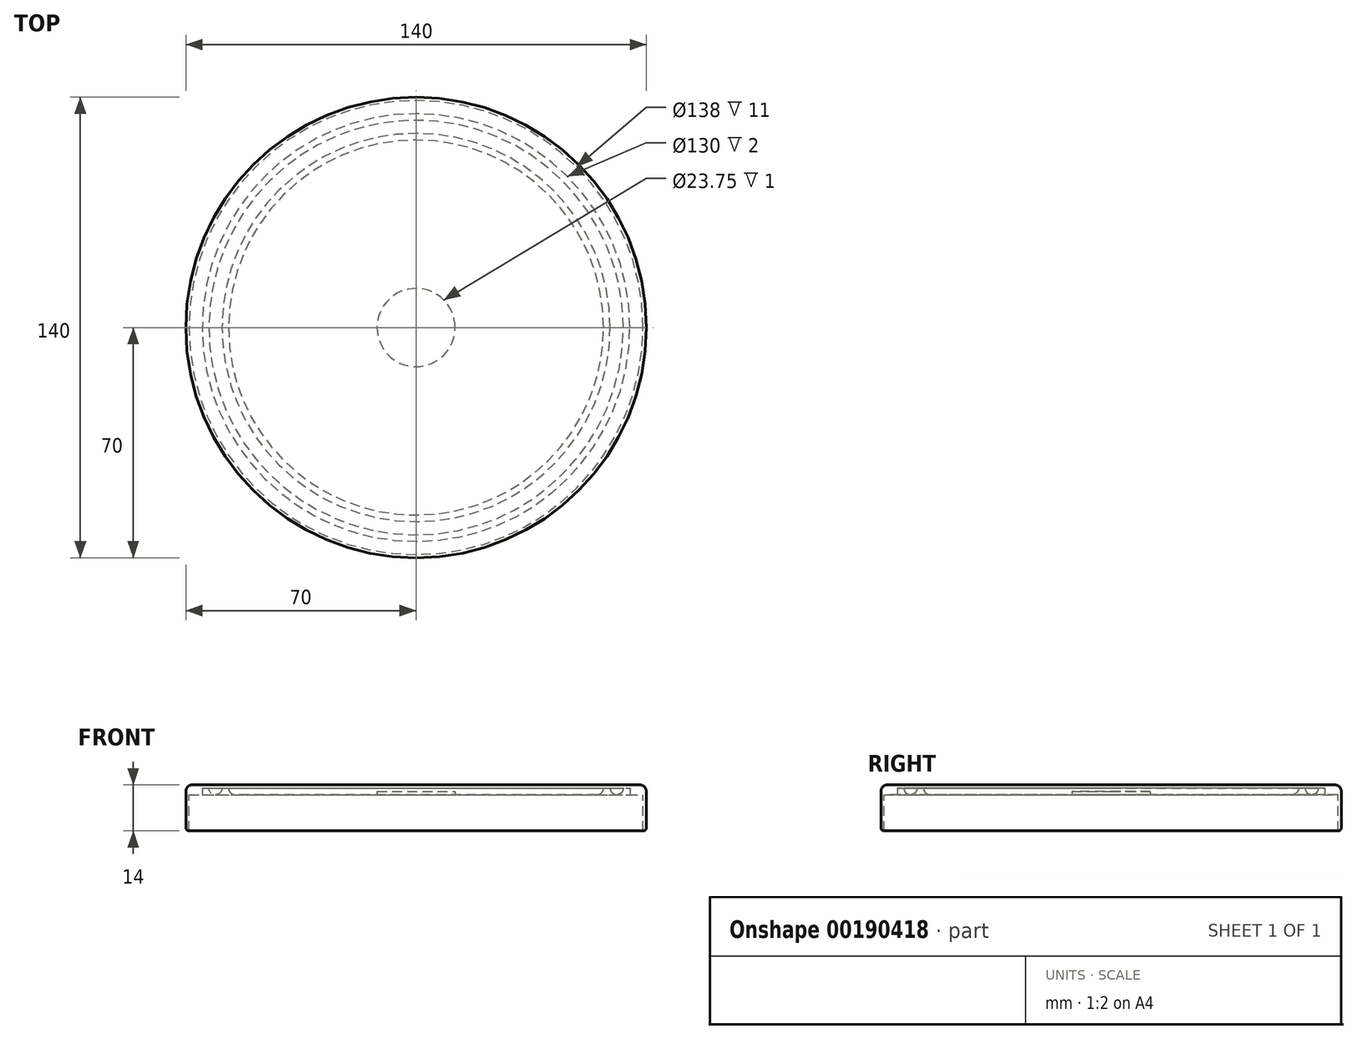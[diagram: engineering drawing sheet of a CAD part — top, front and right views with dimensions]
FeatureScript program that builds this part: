
annotation { "Feature Type Name" : "Feature", "Feature Type Description" : "" }
export const myFeature = defineFeature(function(context is Context, id is Id, definition is map)
    precondition{}
    {
        {
            var Q0;
            Q0=qCreatedBy(makeId("Top.planeOp"),FACE);
            var sketch = newSketch(context, id + "F0", { "sketchPlane" : qUnion([Q0])});
            skCircle(sketch, "E0", {"center": v(0, 0) * mm, "radius": 70 * mm});
            skSolve(sketch);
        }
        {
            var Q0;
            Q0 = qSketchRegion(id + "F0", true);
            extrude(context, id + "F1", {"entities" : qUnion([Q0]), "depth" : 3 * mm});
        }
        {
            var Q0;
            Q0=makeQuery(id+"F1.opExtrude","CAP_FACE",FACE,{"disambiguationData":[OSD([sQuery(id+"F0.wireOp",EDGE,"E0")])],"isStart":true});
            var sketch = newSketch(context, id + "F2", { "sketchPlane" : qUnion([Q0])});
            skCircle(sketch, "E1", {"center": v(0, 0) * mm, "radius": 69 * mm});
            skSolve(sketch);
        }
        {
            var Q0;
            Q0=makeQuery(id+"F2.imprint","IMPRINT",FACE,{"disambiguationData":[TD([[makeQuery(id+"F2.imprint","IMPRINT",EDGE,{"derivedFrom":sQuery(id+"F2.wireOp",EDGE,"E1")}),-1.0]])]});
            extrude(context, id + "F3", {"entities" : qUnion([Q0]), "operationType" : NewBodyOperationType.ADD, "depth" : 11 * mm});
        }
        {
            var Q0;
            Q0=makeQuery(id+"F1.opExtrude","CAP_EDGE",EDGE,{"disambiguationData":[OSD([sQuery(id+"F0.wireOp",EDGE,"E0")])],"isStart":false});
            fillet(context, id + "F4", {"entities" : qUnion([Q0]), "radius" : 2 * mm, "tangentPropagation" : true, "allowEdgeOverflow" : false});
        }
        {
            var Q0;
            Q0=makeQuery(id+"F1.opExtrude","CAP_FACE",FACE,{"disambiguationData":[OSD([sQuery(id+"F0.wireOp",EDGE,"E0")])],"isStart":true});
            var sketch = newSketch(context, id + "F5", { "sketchPlane" : qUnion([Q0])});
            skCircle(sketch, "E2", {"center": v(0, 0) * mm, "radius": 65 * mm});
            skCircle(sketch, "E3", {"center": v(0, 0) * mm, "radius": 63 * mm});
            skCircle(sketch, "E4", {"center": v(0, 0) * mm, "radius": 59 * mm});
            skCircle(sketch, "E5", {"center": v(0, 0) * mm, "radius": 57 * mm});
            skSolve(sketch);
        }
        {
            var Q0;
            Q0=makeQuery(id+"F5.imprint","IMPRINT",FACE,{"disambiguationData":[TD([[makeQuery(id+"F5.imprint","IMPRINT",EDGE,{"derivedFrom":sQuery(id+"F5.wireOp",EDGE,"E2")}),1.0]])]});
            var Q1;
            Q1=makeQuery(id+"F5.imprint","IMPRINT",FACE,{"disambiguationData":[TD([[makeQuery(id+"F5.imprint","IMPRINT",EDGE,{"derivedFrom":sQuery(id+"F5.wireOp",EDGE,"E4")}),1.0]])]});
            extrude(context, id + "F6", {"entities" : qUnion([Q0, Q1]), "operationType" : NewBodyOperationType.REMOVE, "oppositeDirection" : true, "depth" : 2 * mm});
        }
        {
            var Q0;
            Q0=makeQuery(id+"F6.boolean.opBoolean","COPY",EDGE,{"derivedFrom":makeQuery(id+"F6.opExtrude","CAP_EDGE",EDGE,{"disambiguationData":[OSD([sQuery(id+"F5.wireOp",EDGE,"E2")])],"isStart":true})});
            var Q1;
            Q1=makeQuery(id+"F6.boolean.opBoolean","COPY",EDGE,{"derivedFrom":makeQuery(id+"F6.opExtrude","CAP_EDGE",EDGE,{"disambiguationData":[OSD([sQuery(id+"F5.wireOp",EDGE,"E3")])],"isStart":true})});
            var Q2;
            Q2=makeQuery(id+"F6.boolean.opBoolean","COPY",EDGE,{"derivedFrom":makeQuery(id+"F6.opExtrude","CAP_EDGE",EDGE,{"disambiguationData":[OSD([sQuery(id+"F5.wireOp",EDGE,"E4")])],"isStart":true})});
            var Q3;
            Q3=makeQuery(id+"F6.boolean.opBoolean","COPY",EDGE,{"derivedFrom":makeQuery(id+"F6.opExtrude","CAP_EDGE",EDGE,{"disambiguationData":[OSD([sQuery(id+"F5.wireOp",EDGE,"E5")])],"isStart":true})});
            fillet(context, id + "F7", {"entities" : qUnion([Q0, Q1, Q2, Q3]), "radius" : 2 * mm, "tangentPropagation" : true, "allowEdgeOverflow" : false});
        }
        {
            var Q0;
            Q0=makeQuery(id+"F3.opExtrude","CAP_EDGE",EDGE,{"disambiguationData":[OSD([sQuery(id+"F0.wireOp",EDGE,"E0")])],"isStart":false});
            fillet(context, id + "F8", {"entities" : qUnion([Q0]), "radius" : 1 * mm, "tangentPropagation" : true, "allowEdgeOverflow" : false});
        }
        {
            var Q0;
            Q0=makeQuery(id+"F6.boolean.opBoolean","SPLIT",FACE,{"disambiguationData":[TD([makeQuery(id+"F6.opExtrude","SWEPT_FACE",FACE,{"disambiguationData":[OSD([sQuery(id+"F5.wireOp",EDGE,"E5")])]})])],"derivedFrom":makeQuery(id+"F1.opExtrude","CAP_FACE",FACE,{"disambiguationData":[OSD([sQuery(id+"F0.wireOp",EDGE,"E0")])],"isStart":true})});
            var sketch = newSketch(context, id + "F9", { "sketchPlane" : qUnion([Q0])});
            skCircle(sketch, "E6", {"center": v(0, 0) * mm, "radius": 11.88 * mm});
            skSolve(sketch);
        }
        {
            var Q0;
            Q0 = qSketchRegion(id + "F9", true);
            extrude(context, id + "F10", {"entities" : qUnion([Q0]), "operationType" : NewBodyOperationType.REMOVE, "oppositeDirection" : true, "depth" : 1 * mm});
        }
    });
